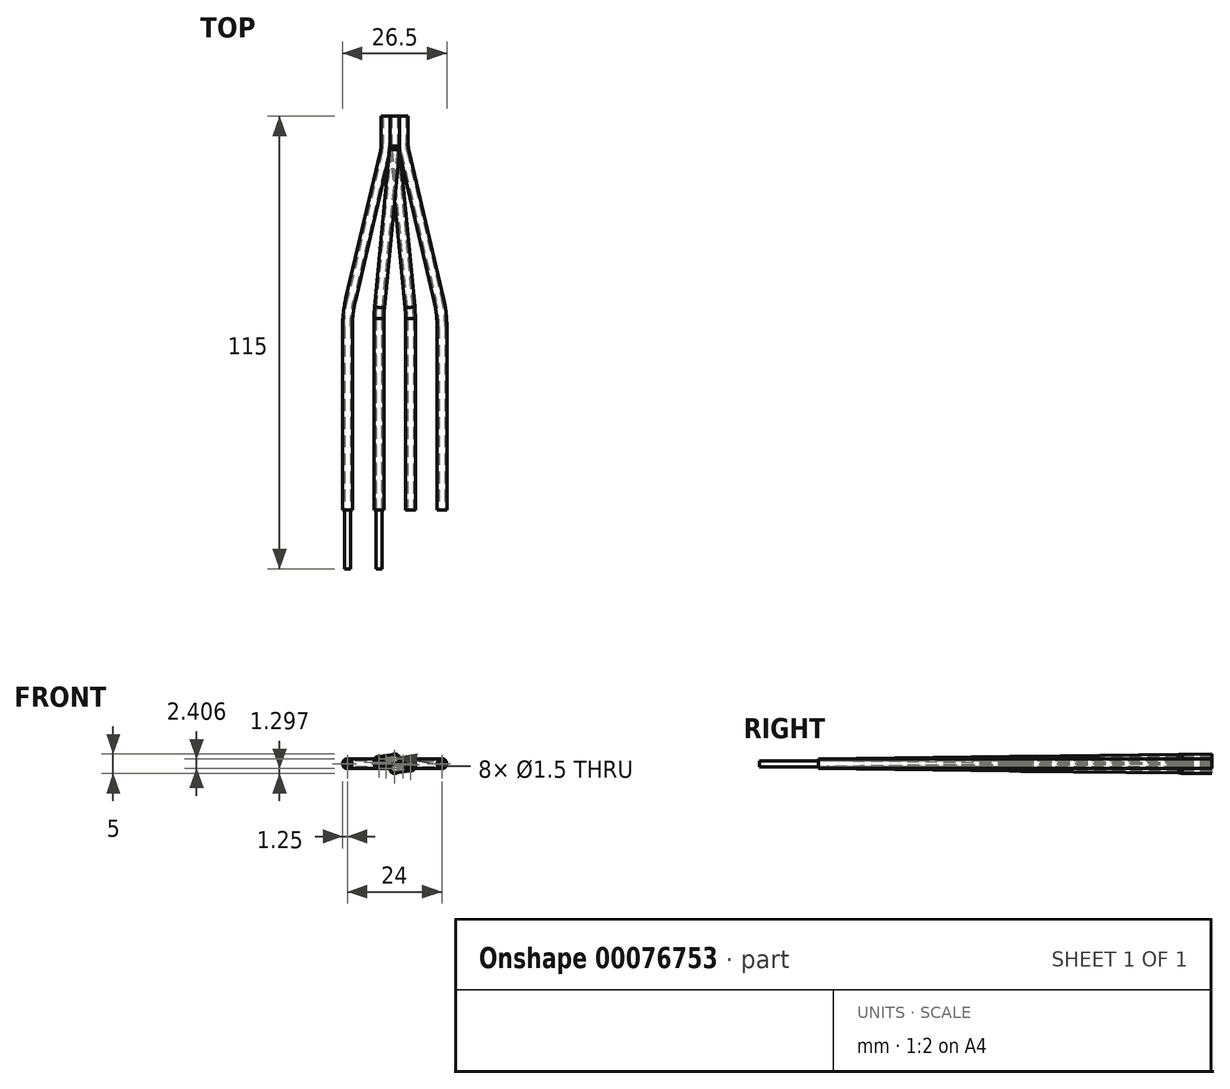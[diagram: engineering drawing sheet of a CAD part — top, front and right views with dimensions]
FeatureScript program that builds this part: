
annotation { "Feature Type Name" : "Feature", "Feature Type Description" : "" }
export const myFeature = defineFeature(function(context is Context, id is Id, definition is map)
    precondition{}
    {
        {
            var Q0;
            Q0=qCreatedBy(makeId("Front.planeOp"),FACE);
            var sketch = newSketch(context, id + "F0", { "sketchPlane" : qUnion([Q0])});
            skCircle(sketch, "E0", {"center": v(0, 1.25) * mm, "radius": 1.25 * mm});
            skCircle(sketch, "E1", {"center": v(0, 1.25) * mm, "radius": 0.75 * mm});
            skCircle(sketch, "E2.MirrorC", {"center": v(0, -1.25) * mm, "radius": 1.25 * mm});
            skCircle(sketch, "E3.MirrorC", {"center": v(0, -1.25) * mm, "radius": 0.75 * mm});
            skCircle(sketch, "E4", {"center": v(2.17, 0) * mm, "radius": 1.25 * mm});
            skCircle(sketch, "E5", {"center": v(2.17, 0) * mm, "radius": 0.75 * mm});
            skCircle(sketch, "E6.MirrorC", {"center": v(-2.17, 0) * mm, "radius": 1.25 * mm});
            skCircle(sketch, "E7.MirrorC", {"center": v(-2.17, 0) * mm, "radius": 0.75 * mm});
            skSolve(sketch);
        }
        {
            var Q0;
            Q0=qCreatedBy(makeId("Front.planeOp"),FACE);
            cPlane(context, id + "F1", {"entities" : qUnion([Q0]), "cplaneType" : CPlaneType.OFFSET, "offset" : 100 * mm, "width" : 150 * mm, "height" : 150 * mm});
        }
        {
            var Q0;
            Q0=qCreatedBy(id+"F1.planeOp",FACE);
            var sketch = newSketch(context, id + "F2", { "sketchPlane" : qUnion([Q0])});
            skCircle(sketch, "E8", {"center": v(-4, 0) * mm, "radius": 0.75 * mm});
            skCircle(sketch, "E9", {"center": v(-12, 0) * mm, "radius": 0.75 * mm});
            skCircle(sketch, "E10.MirrorC", {"center": v(4, 0) * mm, "radius": 0.75 * mm});
            skCircle(sketch, "E11.MirrorC", {"center": v(12, 0) * mm, "radius": 0.75 * mm});
            skSolve(sketch);
        }
        {
            var Q0;
            Q0=qCreatedBy(makeId("Top.planeOp"),FACE);
            var sketch = newSketch(context, id + "F3", { "sketchPlane" : qUnion([Q0])});
            skLineSegment(sketch, "E12", {"start": v(-12, -100) * mm, "end": v(-12, -53.47) * mm});
            skLineSegment(sketch, "E13", {"start": v(-11.2, -46.63) * mm, "end": v(-2.43, -9.12) * mm});
            skLineSegment(sketch, "E14", {"start": v(-2.17, -6.84) * mm, "end": v(-2.17, 0) * mm});
            skPoint(sketch, "E15.visualSharp", {"position": v(-12, -50) * mm});
            skArc(sketch, "E15.filletArc", {"start": v(-11.2, -46.63) * mm, "mid": v(-11.8, -50.02) * mm, "end": v(-12, -53.47) * mm});
            skPoint(sketch, "E16.visualSharp", {"position": v(-2.17, -8) * mm});
            skArc(sketch, "E16.filletArc", {"start": v(-2.43, -9.12) * mm, "mid": v(-2.23, -8) * mm, "end": v(-2.17, -6.84) * mm});
            skLineSegment(sketch, "E17.MirrorCS", {"start": v(12, -100) * mm, "end": v(12, -53.47) * mm});
            skPoint(sketch, "E18.MirrorP", {"position": v(2.17, -8) * mm});
            skArc(sketch, "E19.MirrorCS", {"start": v(11.2, -46.63) * mm, "mid": v(11.8, -50.02) * mm, "end": v(12, -53.47) * mm});
            skLineSegment(sketch, "E20.MirrorCS", {"start": v(2.17, -6.84) * mm, "end": v(2.17, 0) * mm});
            skLineSegment(sketch, "E21.MirrorCS", {"start": v(11.2, -46.63) * mm, "end": v(2.43, -9.12) * mm});
            skArc(sketch, "E22.MirrorCS", {"start": v(2.43, -9.12) * mm, "mid": v(2.23, -8) * mm, "end": v(2.17, -6.84) * mm});
            skPoint(sketch, "E23.MirrorP", {"position": v(12, -50) * mm});
            skSolve(sketch);
        }
        {
            var Q0;
            Q0=sQuery(id+"F2.wireOp",VERTEX,"E10.MirrorC.center");
            var Q1;
            Q1=sQuery(id+"F2.wireOp",VERTEX,"E8.center");
            var Q2;
            Q2=sQuery(id+"F0.wireOp",VERTEX,"E3.MirrorC.center");
            cPlane(context, id + "F4", {"entities" : qUnion([Q0, Q1, Q2]), "cplaneType" : CPlaneType.THREE_POINT, "offset" : 25 * mm, "width" : 150 * mm, "height" : 150 * mm});
        }
        {
            var Q0;
            Q0=qCreatedBy(id+"F4.planeOp",FACE);
            var sketch = newSketch(context, id + "F5", { "sketchPlane" : qUnion([Q0])});
            skLineSegment(sketch, "E24", {"start": v(4, -100) * mm, "end": v(4, -51.42) * mm});
            skLineSegment(sketch, "E25", {"start": v(3.86, -48.57) * mm, "end": v(0.05, -8.47) * mm});
            skLineSegment(sketch, "E26", {"start": v(0, -7.52) * mm, "end": v(0, 0) * mm});
            skPoint(sketch, "E27.visualSharp", {"position": v(4, -50) * mm});
            skArc(sketch, "E27.filletArc", {"start": v(4, -51.42) * mm, "mid": v(3.97, -50) * mm, "end": v(3.86, -48.57) * mm});
            skPoint(sketch, "E28.visualSharp", {"position": v(0, -8) * mm});
            skArc(sketch, "E28.filletArc", {"start": v(0, -7.52) * mm, "mid": v(0.01, -8) * mm, "end": v(0.05, -8.47) * mm});
            skSolve(sketch);
        }
        {
            var Q0;
            Q0=sQuery(id+"F0.wireOp",VERTEX,"E0.center");
            var Q1;
            Q1=sQuery(id+"F2.wireOp",VERTEX,"E8.center");
            var Q2;
            Q2=sQuery(id+"F5.wireOp",VERTEX,"E24.start");
            cPlane(context, id + "F6", {"entities" : qUnion([Q0, Q1, Q2]), "cplaneType" : CPlaneType.THREE_POINT, "offset" : 25 * mm, "width" : 150 * mm, "height" : 150 * mm});
        }
        {
            var Q0;
            Q0=qCreatedBy(id+"F6.planeOp",FACE);
            var sketch = newSketch(context, id + "F7", { "sketchPlane" : qUnion([Q0])});
            skLineSegment(sketch, "E29", {"start": v(0, 0) * mm, "end": v(0, 7.52) * mm});
            skLineSegment(sketch, "E30", {"start": v(-0.05, 8.47) * mm, "end": v(-3.86, 48.57) * mm});
            skLineSegment(sketch, "E31", {"start": v(-4, 51.42) * mm, "end": v(-4, 100) * mm});
            skPoint(sketch, "E32.visualSharp", {"position": v(-4, 50) * mm});
            skArc(sketch, "E32.filletArc", {"start": v(-4, 51.42) * mm, "mid": v(-3.97, 50) * mm, "end": v(-3.86, 48.57) * mm});
            skPoint(sketch, "E33.visualSharp", {"position": v(0, 8) * mm});
            skArc(sketch, "E33.filletArc", {"start": v(0, 7.52) * mm, "mid": v(-0.01, 8) * mm, "end": v(-0.05, 8.47) * mm});
            skSolve(sketch);
        }
        {
            var Q0;
            Q0=makeQuery(id+"F0.imprint","IMPRINT",FACE,{"disambiguationData":[TD([[makeQuery(id+"F0.imprint","IMPRINT",EDGE,{"derivedFrom":sQuery(id+"F0.wireOp",EDGE,"E1")}),1.0]])]});
            var Q1;
            Q1=sQuery(id+"F7.wireOp",EDGE,"E31");
            var Q2;
            Q2=sQuery(id+"F7.wireOp",EDGE,"E32.filletArc");
            var Q3;
            Q3=sQuery(id+"F7.wireOp",EDGE,"E30");
            var Q4;
            Q4=sQuery(id+"F7.wireOp",EDGE,"E33.filletArc");
            var Q5;
            Q5=sQuery(id+"F7.wireOp",EDGE,"E29");
            sweep(context, id + "F8", {"profiles" : qUnion([Q0]), "path" : qUnion([Q1, Q2, Q3, Q4, Q5]), "keepProfileOrientation" : true});
        }
        {
            var Q0;
            Q0=makeQuery(id+"F0.imprint","IMPRINT",FACE,{"disambiguationData":[TD([[makeQuery(id+"F0.imprint","IMPRINT",EDGE,{"derivedFrom":sQuery(id+"F0.wireOp",EDGE,"E7.MirrorC")}),-1.0]])]});
            var Q1;
            Q1=sQuery(id+"F3.wireOp",EDGE,"E14");
            var Q2;
            Q2=sQuery(id+"F3.wireOp",EDGE,"E16.filletArc");
            var Q3;
            Q3=sQuery(id+"F3.wireOp",EDGE,"E13");
            var Q4;
            Q4=sQuery(id+"F3.wireOp",EDGE,"E15.filletArc");
            var Q5;
            Q5=sQuery(id+"F3.wireOp",EDGE,"E12");
            sweep(context, id + "F9", {"profiles" : qUnion([Q0]), "path" : qUnion([Q1, Q2, Q3, Q4, Q5])});
        }
        {
            var Q0;
            Q0=makeQuery(id+"F0.imprint","IMPRINT",FACE,{"disambiguationData":[TD([[makeQuery(id+"F0.imprint","IMPRINT",EDGE,{"derivedFrom":sQuery(id+"F0.wireOp",EDGE,"E3.MirrorC")}),-1.0]])]});
            var Q1;
            Q1=sQuery(id+"F5.wireOp",EDGE,"E26");
            var Q2;
            Q2=sQuery(id+"F5.wireOp",EDGE,"E28.filletArc");
            var Q3;
            Q3=sQuery(id+"F5.wireOp",EDGE,"E25");
            var Q4;
            Q4=sQuery(id+"F5.wireOp",EDGE,"E27.filletArc");
            var Q5;
            Q5=sQuery(id+"F5.wireOp",EDGE,"E24");
            sweep(context, id + "F10", {"profiles" : qUnion([Q0]), "path" : qUnion([Q1, Q2, Q3, Q4, Q5])});
        }
        {
            var Q0;
            Q0=makeQuery(id+"F0.imprint","IMPRINT",FACE,{"disambiguationData":[TD([[makeQuery(id+"F0.imprint","IMPRINT",EDGE,{"derivedFrom":sQuery(id+"F0.wireOp",EDGE,"E5")}),1.0]])]});
            var Q1;
            Q1=sQuery(id+"F3.wireOp",EDGE,"E20.MirrorCS");
            var Q2;
            Q2=sQuery(id+"F3.wireOp",EDGE,"E22.MirrorCS");
            var Q3;
            Q3=sQuery(id+"F3.wireOp",EDGE,"E21.MirrorCS");
            var Q4;
            Q4=sQuery(id+"F3.wireOp",EDGE,"E19.MirrorCS");
            var Q5;
            Q5=sQuery(id+"F3.wireOp",EDGE,"E17.MirrorCS");
            sweep(context, id + "F11", {"profiles" : qUnion([Q0]), "path" : qUnion([Q1, Q2, Q3, Q4, Q5])});
        }
        {
            var Q0;
            Q0=makeQuery(id+"F0.imprint","IMPRINT",FACE,{"disambiguationData":[TD([[makeQuery(id+"F0.imprint","IMPRINT",EDGE,{"derivedFrom":sQuery(id+"F0.wireOp",EDGE,"E5")}),-1.0]])]});
            var Q1;
            Q1=sQuery(id+"F3.wireOp",EDGE,"E20.MirrorCS");
            var Q2;
            Q2=sQuery(id+"F3.wireOp",EDGE,"E22.MirrorCS");
            var Q3;
            Q3=sQuery(id+"F3.wireOp",EDGE,"E21.MirrorCS");
            var Q4;
            Q4=sQuery(id+"F3.wireOp",EDGE,"E19.MirrorCS");
            var Q5;
            Q5=sQuery(id+"F3.wireOp",EDGE,"E17.MirrorCS");
            sweep(context, id + "F12", {"profiles" : qUnion([Q0]), "path" : qUnion([Q1, Q2, Q3, Q4, Q5])});
        }
        {
            var Q0;
            Q0=makeQuery(id+"F2.imprint","IMPRINT",FACE,{"disambiguationData":[TD([[makeQuery(id+"F2.imprint","IMPRINT",EDGE,{"derivedFrom":sQuery(id+"F2.wireOp",EDGE,"E11.MirrorC")}),-1.0]])]});
            var Q1;
            Q1=makeQuery(id+"F2.imprint","IMPRINT",FACE,{"disambiguationData":[TD([[makeQuery(id+"F2.imprint","IMPRINT",EDGE,{"derivedFrom":sQuery(id+"F2.wireOp",EDGE,"E10.MirrorC")}),-1.0]])]});
            var Q2;
            Q2=makeQuery(id+"F2.imprint","IMPRINT",FACE,{"disambiguationData":[TD([[makeQuery(id+"F2.imprint","IMPRINT",EDGE,{"derivedFrom":sQuery(id+"F2.wireOp",EDGE,"E8")}),1.0]])]});
            var Q3;
            Q3=makeQuery(id+"F2.imprint","IMPRINT",FACE,{"disambiguationData":[TD([[makeQuery(id+"F2.imprint","IMPRINT",EDGE,{"derivedFrom":sQuery(id+"F2.wireOp",EDGE,"E9")}),1.0]])]});
            var Q4;
            Q4=sQuery(id+"F2.wireOp",EDGE,"E11.MirrorC");
            extrude(context, id + "F13", {"entities" : qUnion([Q0, Q1, Q2, Q3]), "operationType" : NewBodyOperationType.ADD, "surfaceEntities" : qUnion([Q4]), "depth" : 15 * mm, "offsetDistance" : 25 * mm});
        }
        {
            var Q0;
            Q0=makeQuery(id+"F0.imprint","IMPRINT",FACE,{"disambiguationData":[TD([[makeQuery(id+"F0.imprint","IMPRINT",EDGE,{"derivedFrom":sQuery(id+"F0.wireOp",EDGE,"E7.MirrorC")}),1.0]])]});
            var Q1;
            Q1=sQuery(id+"F3.wireOp",EDGE,"E14");
            var Q2;
            Q2=sQuery(id+"F3.wireOp",EDGE,"E16.filletArc");
            var Q3;
            Q3=sQuery(id+"F3.wireOp",EDGE,"E13");
            var Q4;
            Q4=sQuery(id+"F3.wireOp",EDGE,"E15.filletArc");
            var Q5;
            Q5=sQuery(id+"F3.wireOp",EDGE,"E12");
            sweep(context, id + "F14", {"profiles" : qUnion([Q0]), "path" : qUnion([Q1, Q2, Q3, Q4, Q5])});
        }
        {
            var Q0;
            Q0=makeQuery(id+"F0.imprint","IMPRINT",FACE,{"disambiguationData":[TD([[makeQuery(id+"F0.imprint","IMPRINT",EDGE,{"derivedFrom":sQuery(id+"F0.wireOp",EDGE,"E3.MirrorC")}),1.0]])]});
            var Q1;
            Q1=sQuery(id+"F5.wireOp",EDGE,"E26");
            var Q2;
            Q2=sQuery(id+"F5.wireOp",EDGE,"E28.filletArc");
            var Q3;
            Q3=sQuery(id+"F5.wireOp",EDGE,"E25");
            var Q4;
            Q4=sQuery(id+"F5.wireOp",EDGE,"E24");
            var Q5;
            Q5=sQuery(id+"F5.wireOp",EDGE,"E27.filletArc");
            sweep(context, id + "F15", {"profiles" : qUnion([Q0]), "path" : qUnion([Q1, Q2, Q3, Q4, Q5])});
        }
        {
            var Q0;
            Q0=makeQuery(id+"F0.imprint","IMPRINT",FACE,{"disambiguationData":[TD([[makeQuery(id+"F0.imprint","IMPRINT",EDGE,{"derivedFrom":sQuery(id+"F0.wireOp",EDGE,"E1")}),-1.0]])]});
            var Q1;
            Q1=sQuery(id+"F7.wireOp",EDGE,"E29");
            var Q2;
            Q2=sQuery(id+"F7.wireOp",EDGE,"E33.filletArc");
            var Q3;
            Q3=sQuery(id+"F7.wireOp",EDGE,"E30");
            var Q4;
            Q4=sQuery(id+"F7.wireOp",EDGE,"E32.filletArc");
            var Q5;
            Q5=sQuery(id+"F7.wireOp",EDGE,"E31");
            sweep(context, id + "F16", {"profiles" : qUnion([Q0]), "path" : qUnion([Q1, Q2, Q3, Q4, Q5])});
        }
    });
